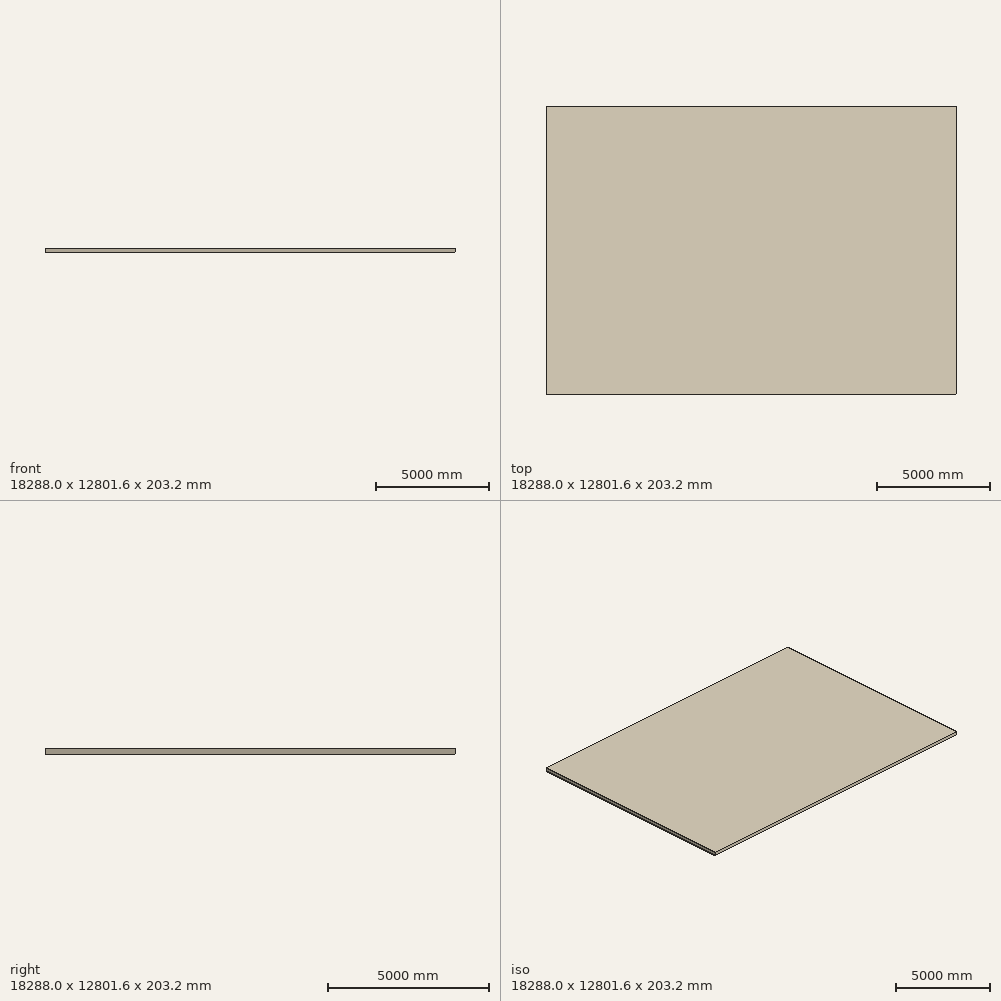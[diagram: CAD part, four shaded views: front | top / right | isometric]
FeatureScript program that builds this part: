
annotation { "Feature Type Name" : "Feature", "Feature Type Description" : "" }
export const myFeature = defineFeature(function(context is Context, id is Id, definition is map)
    precondition{}
    {
        {
            var Q0;
            Q0=qCreatedBy(makeId("Top.planeOp"),FACE);
            var sketch = newSketch(context, id + "F0", { "sketchPlane" : qUnion([Q0])});
            skLineSegment(sketch, "E0.bottom", {"start": v(-9144, 6400.8) * mm, "end": v(9144, 6400.8) * mm});
            skLineSegment(sketch, "E0.top", {"start": v(-9144, -6400.8) * mm, "end": v(9144, -6400.8) * mm});
            skLineSegment(sketch, "E0.left", {"start": v(-9144, 6400.8) * mm, "end": v(-9144, -6400.8) * mm});
            skLineSegment(sketch, "E0.right", {"start": v(9144, 6400.8) * mm, "end": v(9144, -6400.8) * mm});
            skLineSegment(sketch, "E1", {"start": v(-9144, -6400.8) * mm, "end": v(9144, 6400.8) * mm, "construction": true});
            skSolve(sketch);
        }
        {
            var Q0;
            Q0 = qSketchRegion(id + "F0", true);
            extrude(context, id + "F1", {"entities" : qUnion([Q0]), "depth" : 203.2 * mm, "offsetDistance" : 25.4 * mm});
        }
    });
